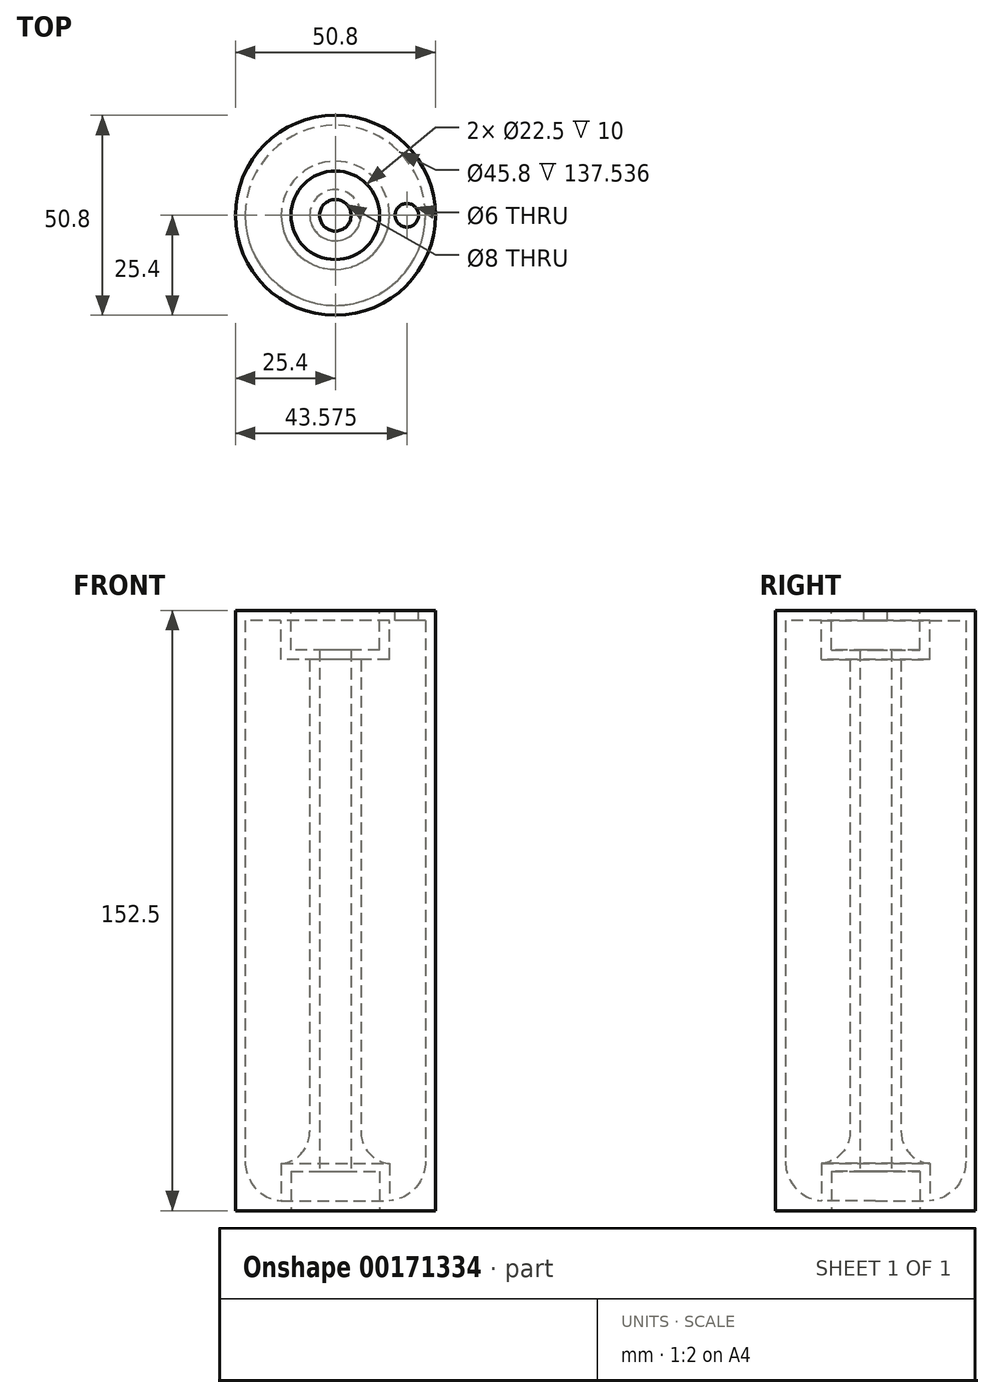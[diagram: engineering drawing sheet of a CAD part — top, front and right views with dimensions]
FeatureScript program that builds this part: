
annotation { "Feature Type Name" : "Feature", "Feature Type Description" : "" }
export const myFeature = defineFeature(function(context is Context, id is Id, definition is map)
    precondition{}
    {
        {
            var Q0;
            Q0=qCreatedBy(makeId("Top.planeOp"),FACE);
            var sketch = newSketch(context, id + "F0", { "sketchPlane" : qUnion([Q0])});
            skCircle(sketch, "E0", {"center": v(0, 0) * mm, "radius": 25.4 * mm});
            skSolve(sketch);
        }
        {
            var Q0;
            Q0=makeQuery(id+"F0.imprint","IMPRINT",FACE,{"disambiguationData":[TD([[makeQuery(id+"F0.imprint","IMPRINT",EDGE,{"derivedFrom":sQuery(id+"F0.wireOp",EDGE,"E0")}),1.0]])]});
            extrude(context, id + "F1", {"entities" : qUnion([Q0]), "depth" : 152.5 * mm});
        }
        {
            var Q0;
            Q0=makeQuery(id+"F1.opExtrude","CAP_FACE",FACE,{"disambiguationData":[OSD([sQuery(id+"F0.wireOp",EDGE,"E0")])],"isStart":false});
            shell(context, id + "F2", {"entities" : qUnion([Q0]), "thickness" : 2.5 * mm});
        }
        {
            var Q0;
            {var subQ0=sQuery(id+"F0.wireOp",EDGE,"E0");Q0=makeQuery(id+"F2.opShell","OFFSET_FACE",FACE,{"disambiguationData":[OSD([subQ0]),TDD([makeQuery(id+"F1.opExtrude","CAP_FACE",FACE,{"disambiguationData":[OSD([subQ0])],"isStart":true})])]});}
            var sketch = newSketch(context, id + "F3", { "sketchPlane" : qUnion([Q0])});
            skCircle(sketch, "E1", {"center": v(0, 0) * mm, "radius": 6.5 * mm});
            skSolve(sketch);
        }
        {
            var Q0;
            Q0=makeQuery(id+"F3.imprint","IMPRINT",FACE,{"disambiguationData":[TD([[makeQuery(id+"F3.imprint","IMPRINT",EDGE,{"derivedFrom":sQuery(id+"F3.wireOp",EDGE,"E1")}),1.0]])]});
            extrude(context, id + "F4", {"entities" : qUnion([Q0]), "operationType" : NewBodyOperationType.ADD, "depth" : 150 * mm});
        }
        {
            var Q0;
            Q0=makeQuery(id+"F4.opExtrude","CAP_FACE",FACE,{"disambiguationData":[OSD([sQuery(id+"F3.wireOp",EDGE,"E1")])],"isStart":false});
            shell(context, id + "F5", {"entities" : qUnion([Q0]), "thickness" : 2.5 * mm});
        }
        {
            var Q0;
            Q0=makeQuery(id+"F1.opExtrude","CAP_FACE",FACE,{"disambiguationData":[OSD([sQuery(id+"F0.wireOp",EDGE,"E0")])],"isStart":true});
            var sketch = newSketch(context, id + "F6", { "sketchPlane" : qUnion([Q0])});
            skCircle(sketch, "E2", {"center": v(0, 0) * mm, "radius": 13.75 * mm});
            skSolve(sketch);
        }
        {
            var Q0;
            Q0=makeQuery(id+"F6.imprint","IMPRINT",FACE,{"disambiguationData":[TD([[makeQuery(id+"F6.imprint","IMPRINT",EDGE,{"derivedFrom":sQuery(id+"F6.wireOp",EDGE,"E2")}),1.0]])]});
            extrude(context, id + "F7", {"entities" : qUnion([Q0]), "operationType" : NewBodyOperationType.ADD, "oppositeDirection" : true, "depth" : 12 * mm});
        }
        {
            var Q0;
            Q0=makeQuery(id+"F1.opExtrude","CAP_FACE",FACE,{"disambiguationData":[OSD([sQuery(id+"F0.wireOp",EDGE,"E0")])],"isStart":true});
            var sketch = newSketch(context, id + "F8", { "sketchPlane" : qUnion([Q0])});
            skCircle(sketch, "E3", {"center": v(0, 0) * mm, "radius": 11.25 * mm});
            skSolve(sketch);
        }
        {
            var Q0;
            {var subQ0=sQuery(id+"F0.wireOp",EDGE,"E0");Q0=makeQuery(id+"F2.opShell","OFFSET_EDGE",EDGE,{"disambiguationData":[OSD([subQ0]),TDD([makeQuery(id+"F1.opExtrude","CAP_EDGE",EDGE,{"disambiguationData":[OSD([subQ0])],"isStart":true})])]});}
            fillet(context, id + "F9", {"entities" : qUnion([Q0]), "radius" : 10 * mm, "tangentPropagation" : true, "allowEdgeOverflow" : false});
        }
        {
            var Q0;
            Q0=makeQuery(id+"F7.boolean.opBoolean","INTERSECT",EDGE,{"derivedFrom":[makeQuery(id+"F4.opExtrude","SWEPT_FACE",FACE,{"disambiguationData":[OSD([sQuery(id+"F3.wireOp",EDGE,"E1")])]}),makeQuery(id+"F7.opExtrude","CAP_FACE",FACE,{"disambiguationData":[OSD([sQuery(id+"F6.wireOp",EDGE,"E2")])],"isStart":false})]});
            fillet(context, id + "F10", {"entities" : qUnion([Q0]), "radius" : 8 * mm, "tangentPropagation" : true, "allowEdgeOverflow" : false});
        }
        {
            var Q0;
            Q0=makeQuery(id+"F8.imprint","IMPRINT",FACE,{"disambiguationData":[TD([[makeQuery(id+"F8.imprint","IMPRINT",EDGE,{"derivedFrom":sQuery(id+"F8.wireOp",EDGE,"E3")}),1.0]])]});
            extrude(context, id + "F11", {"entities" : qUnion([Q0]), "operationType" : NewBodyOperationType.REMOVE, "oppositeDirection" : true, "depth" : 10 * mm});
        }
        {
            var Q0;
            Q0=makeQuery(id+"F1.opExtrude","CAP_FACE",FACE,{"disambiguationData":[OSD([sQuery(id+"F0.wireOp",EDGE,"E0")])],"isStart":false});
            var sketch = newSketch(context, id + "F12", { "sketchPlane" : qUnion([Q0])});
            skCircle(sketch, "E4.0", {"center": v(0, 0) * mm, "radius": 25.4 * mm});
            skSolve(sketch);
        }
        {
            var Q0;
            Q0 = qSketchRegion(id + "F12", true);
            extrude(context, id + "F13", {"entities" : qUnion([Q0]), "operationType" : NewBodyOperationType.ADD, "oppositeDirection" : true, "depth" : 2.5 * mm});
        }
        {
            var Q0;
            Q0=makeQuery(id+"F13.boolean.opBoolean","MERGE",FACE,{"derivedFrom":[makeQuery(id+"F1.opExtrude","CAP_FACE",FACE,{"disambiguationData":[OSD([sQuery(id+"F0.wireOp",EDGE,"E0")])],"isStart":false}),makeQuery(id+"F4.opExtrude","CAP_FACE",FACE,{"disambiguationData":[OSD([sQuery(id+"F3.wireOp",EDGE,"E1")])],"isStart":false}),makeQuery(id+"F13.opExtrude","CAP_FACE",FACE,{"disambiguationData":[OSD([sQuery(id+"F12.wireOp",EDGE,"E4.0")])],"isStart":true})]});
            var sketch = newSketch(context, id + "F14", { "sketchPlane" : qUnion([Q0])});
            skCircle(sketch, "E5", {"center": v(0, 0) * mm, "radius": 13.75 * mm});
            skSolve(sketch);
        }
        {
            var Q0;
            Q0=makeQuery(id+"F14.imprint","IMPRINT",FACE,{"disambiguationData":[TD([[makeQuery(id+"F14.imprint","IMPRINT",EDGE,{"derivedFrom":sQuery(id+"F14.wireOp",EDGE,"E5")}),1.0]])]});
            extrude(context, id + "F15", {"entities" : qUnion([Q0]), "operationType" : NewBodyOperationType.ADD, "oppositeDirection" : true, "depth" : 12.5 * mm});
        }
        {
            var Q0;
            Q0=makeQuery(id+"F13.boolean.opBoolean","MERGE",FACE,{"derivedFrom":[makeQuery(id+"F1.opExtrude","CAP_FACE",FACE,{"disambiguationData":[OSD([sQuery(id+"F0.wireOp",EDGE,"E0")])],"isStart":false}),makeQuery(id+"F4.opExtrude","CAP_FACE",FACE,{"disambiguationData":[OSD([sQuery(id+"F3.wireOp",EDGE,"E1")])],"isStart":false}),makeQuery(id+"F13.opExtrude","CAP_FACE",FACE,{"disambiguationData":[OSD([sQuery(id+"F12.wireOp",EDGE,"E4.0")])],"isStart":true})]});
            var sketch = newSketch(context, id + "F16", { "sketchPlane" : qUnion([Q0])});
            skCircle(sketch, "E6", {"center": v(0, 0) * mm, "radius": 11.25 * mm});
            skSolve(sketch);
        }
        {
            var Q0;
            Q0=makeQuery(id+"F16.imprint","IMPRINT",FACE,{"disambiguationData":[TD([[makeQuery(id+"F16.imprint","IMPRINT",EDGE,{"derivedFrom":sQuery(id+"F16.wireOp",EDGE,"E6")}),1.0]])]});
            extrude(context, id + "F17", {"entities" : qUnion([Q0]), "operationType" : NewBodyOperationType.REMOVE, "oppositeDirection" : true, "depth" : 10 * mm});
        }
        {
            var Q0;
            Q0=makeQuery(id+"F17.boolean.opBoolean","COPY",FACE,{"derivedFrom":makeQuery(id+"F17.opExtrude","CAP_FACE",FACE,{"disambiguationData":[OSD([sQuery(id+"F16.wireOp",EDGE,"E6")])],"isStart":false})});
            var sketch = newSketch(context, id + "F18", { "sketchPlane" : qUnion([Q0])});
            skCircle(sketch, "E7", {"center": v(0, 0) * mm, "radius": 4 * mm});
            skSolve(sketch);
        }
        {
            var Q0;
            Q0 = qSketchRegion(id + "F18", true);
            extrude(context, id + "F19", {"entities" : qUnion([Q0]), "operationType" : NewBodyOperationType.REMOVE, "endBound" : BoundingType.THROUGH_ALL, "oppositeDirection" : true, "depth" : 25 * mm});
        }
        {
            var Q0;
            Q0=makeQuery(id+"F13.boolean.opBoolean","MERGE",FACE,{"derivedFrom":[makeQuery(id+"F1.opExtrude","CAP_FACE",FACE,{"disambiguationData":[OSD([sQuery(id+"F0.wireOp",EDGE,"E0")])],"isStart":false}),makeQuery(id+"F4.opExtrude","CAP_FACE",FACE,{"disambiguationData":[OSD([sQuery(id+"F3.wireOp",EDGE,"E1")])],"isStart":false}),makeQuery(id+"F13.opExtrude","CAP_FACE",FACE,{"disambiguationData":[OSD([sQuery(id+"F12.wireOp",EDGE,"E4.0")])],"isStart":true})]});
            var sketch = newSketch(context, id + "F20", { "sketchPlane" : qUnion([Q0])});
            skCircle(sketch, "E8", {"center": v(18.17, 0) * mm, "radius": 3 * mm});
            skSolve(sketch);
        }
        {
            var Q0;
            Q0 = qSketchRegion(id + "F20", true);
            extrude(context, id + "F21", {"entities" : qUnion([Q0]), "operationType" : NewBodyOperationType.REMOVE, "oppositeDirection" : true, "depth" : 25 * mm});
        }
    });
